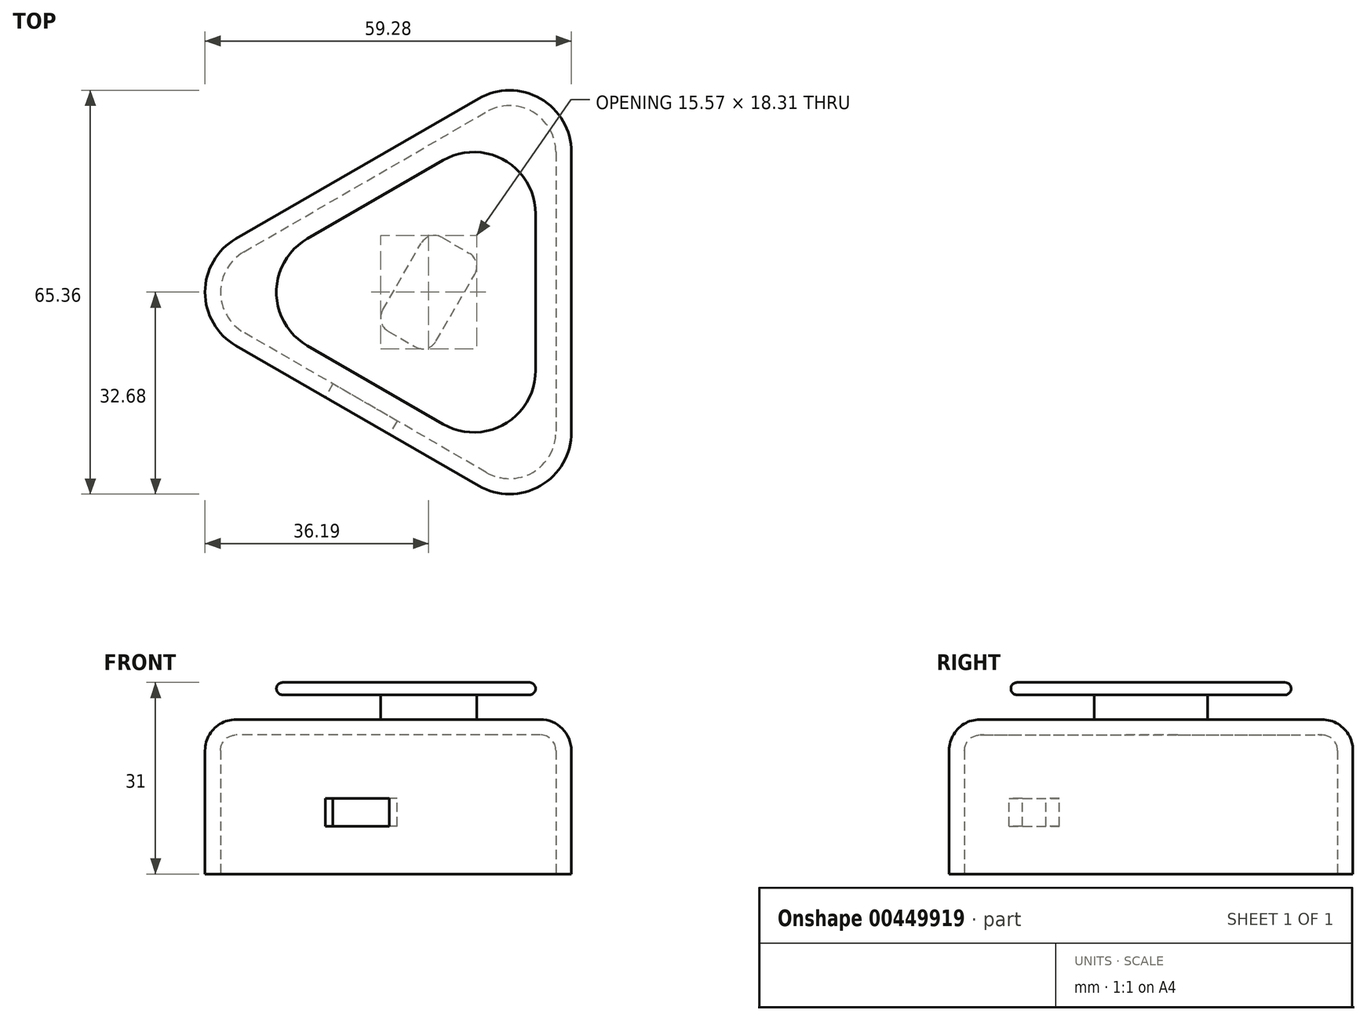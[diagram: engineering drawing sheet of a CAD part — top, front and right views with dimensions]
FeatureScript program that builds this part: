
annotation { "Feature Type Name" : "Feature", "Feature Type Description" : "" }
export const myFeature = defineFeature(function(context is Context, id is Id, definition is map)
    precondition{}
    {
        {
            var Q0;
            Q0=qCreatedBy(makeId("Top.planeOp"),FACE);
            var sketch = newSketch(context, id + "F0", { "sketchPlane" : qUnion([Q0])});
            skCircle(sketch, "E0.cCircle", {"center": v(0, 0) * mm, "radius": 23.1 * mm, "construction": true});
            skLineSegment(sketch, "E0.0", {"start": v(23.1, 40) * mm, "end": v(23.1, -40) * mm});
            skLineSegment(sketch, "E0.1", {"start": v(23.1, -40) * mm, "end": v(-46.19, 0) * mm});
            skLineSegment(sketch, "E0.2", {"start": v(-46.19, 0) * mm, "end": v(23.1, 40) * mm});
            skPoint(sketch, "E0.0.midPoint", {"position": v(23.1, 0) * mm});
            skSolve(sketch);
        }
        {
            var Q0;
            Q0=makeQuery(id+"F0.imprint","IMPRINT",FACE,{"disambiguationData":[TD([[makeQuery(id+"F0.imprint","IMPRINT",EDGE,{"derivedFrom":sQuery(id+"F0.wireOp",EDGE,"E0.0")}),-1.0]])]});
            extrude(context, id + "F1", {"entities" : qUnion([Q0]), "depth" : 25 * mm, "offsetDistance" : 25 * mm});
        }
        {
            var Q0;
            Q0=makeQuery(id+"F1.opExtrude","SWEPT_EDGE",EDGE,{"disambiguationData":[OSD([sQuery(id+"F0.wireOp",EDGE,"E0.1"),sQuery(id+"F0.wireOp",EDGE,"E0.2")])]});
            var Q1;
            Q1=makeQuery(id+"F1.opExtrude","SWEPT_EDGE",EDGE,{"disambiguationData":[OSD([sQuery(id+"F0.wireOp",EDGE,"E0.0"),sQuery(id+"F0.wireOp",EDGE,"E0.1")])]});
            var Q2;
            Q2=makeQuery(id+"F1.opExtrude","SWEPT_EDGE",EDGE,{"disambiguationData":[OSD([sQuery(id+"F0.wireOp",EDGE,"E0.0"),sQuery(id+"F0.wireOp",EDGE,"E0.2")])]});
            fillet(context, id + "F2", {"entities" : qUnion([Q0, Q1, Q2]), "radius" : 10 * mm, "tangentPropagation" : true, "allowEdgeOverflow" : false});
        }
        {
            var Q0;
            Q0=makeQuery(id+"F1.opExtrude","CAP_EDGE",EDGE,{"disambiguationData":[OSD([sQuery(id+"F0.wireOp",EDGE,"E0.1")])],"isStart":false});
            fillet(context, id + "F3", {"entities" : qUnion([Q0]), "radius" : 5 * mm, "tangentPropagation" : true, "allowEdgeOverflow" : false});
        }
        {
            var Q0;
            Q0=makeQuery(id+"F1.opExtrude","CAP_FACE",FACE,{"disambiguationData":[OSD([sQuery(id+"F0.wireOp",EDGE,"E0.0"),sQuery(id+"F0.wireOp",EDGE,"E0.1"),sQuery(id+"F0.wireOp",EDGE,"E0.2")])],"isStart":true});
            shell(context, id + "F4", {"entities" : qUnion([Q0]), "thickness" : 2.5 * mm});
        }
        {
            var Q0;
            Q0=makeQuery(id+"F1.opExtrude","CAP_FACE",FACE,{"disambiguationData":[OSD([sQuery(id+"F0.wireOp",EDGE,"E0.0"),sQuery(id+"F0.wireOp",EDGE,"E0.1"),sQuery(id+"F0.wireOp",EDGE,"E0.2")])],"isStart":false});
            var sketch = newSketch(context, id + "F5", { "sketchPlane" : qUnion([Q0])});
            skLineSegment(sketch, "E1.bottom", {"start": v(-8.7, -5.08) * mm, "end": v(0.04, 10.08) * mm});
            skLineSegment(sketch, "E1.top", {"start": v(-0.04, -10.08) * mm, "end": v(8.7, 5.08) * mm});
            skLineSegment(sketch, "E1.left", {"start": v(-8.7, -5.08) * mm, "end": v(-0.04, -10.08) * mm});
            skLineSegment(sketch, "E1.right", {"start": v(0.04, 10.08) * mm, "end": v(8.7, 5.08) * mm});
            skPoint(sketch, "E1.middle", {"position": v(0, 0) * mm});
            skSolve(sketch);
        }
        {
            var Q0;
            Q0=makeQuery(id+"F5.imprint","IMPRINT",FACE,{"disambiguationData":[TD([[makeQuery(id+"F5.imprint","IMPRINT",EDGE,{"derivedFrom":sQuery(id+"F5.wireOp",EDGE,"E1.bottom")}),-1.0]])]});
            extrude(context, id + "F6", {"entities" : qUnion([Q0]), "operationType" : NewBodyOperationType.ADD, "depth" : 4 * mm, "offsetDistance" : 25 * mm});
        }
        {
            var Q0;
            Q0=makeQuery(id+"F6.opExtrude","SWEPT_EDGE",EDGE,{"disambiguationData":[OSD([sQuery(id+"F5.wireOp",EDGE,"E1.top"),sQuery(id+"F5.wireOp",EDGE,"E1.right")])]});
            var Q1;
            Q1=makeQuery(id+"F6.opExtrude","SWEPT_EDGE",EDGE,{"disambiguationData":[OSD([sQuery(id+"F5.wireOp",EDGE,"E1.bottom"),sQuery(id+"F5.wireOp",EDGE,"E1.right")])]});
            var Q2;
            Q2=makeQuery(id+"F6.opExtrude","SWEPT_EDGE",EDGE,{"disambiguationData":[OSD([sQuery(id+"F5.wireOp",EDGE,"E1.top"),sQuery(id+"F5.wireOp",EDGE,"E1.left")])]});
            var Q3;
            Q3=makeQuery(id+"F6.opExtrude","SWEPT_EDGE",EDGE,{"disambiguationData":[OSD([sQuery(id+"F5.wireOp",EDGE,"E1.bottom"),sQuery(id+"F5.wireOp",EDGE,"E1.left")])]});
            fillet(context, id + "F7", {"entities" : qUnion([Q0, Q1, Q2, Q3]), "radius" : 2.5 * mm, "tangentPropagation" : true, "allowEdgeOverflow" : false});
        }
        {
            var Q0;
            Q0=makeQuery(id+"F6.opExtrude","CAP_FACE",FACE,{"disambiguationData":[OSD([sQuery(id+"F5.wireOp",EDGE,"E1.bottom"),sQuery(id+"F5.wireOp",EDGE,"E1.top"),sQuery(id+"F5.wireOp",EDGE,"E1.left"),sQuery(id+"F5.wireOp",EDGE,"E1.right")])],"isStart":false});
            var sketch = newSketch(context, id + "F8", { "sketchPlane" : qUnion([Q0])});
            skCircle(sketch, "E2.cCircle", {"center": v(0, 0) * mm, "radius": 17.32 * mm, "construction": true});
            skLineSegment(sketch, "E2.0", {"start": v(17.32, 30) * mm, "end": v(17.32, -30) * mm});
            skLineSegment(sketch, "E2.1", {"start": v(17.32, -30) * mm, "end": v(-34.64, 0) * mm});
            skLineSegment(sketch, "E2.2", {"start": v(-34.64, 0) * mm, "end": v(17.32, 30) * mm});
            skPoint(sketch, "E2.0.midPoint", {"position": v(17.32, 0) * mm});
            skSolve(sketch);
        }
        {
            var Q0;
            Q0=makeQuery(id+"F8.imprint","IMPRINT",FACE,{"disambiguationData":[TD([[makeQuery(id+"F8.imprint","IMPRINT",EDGE,{"derivedFrom":sQuery(id+"F8.wireOp",EDGE,"E2.0")}),-1.0]])]});
            var Q1;
            {var subQ3=sQuery(id+"F5.wireOp",EDGE,"E1.bottom");Q1=makeQuery(id+"F8.imprint","IMPRINT",FACE,{"disambiguationData":[TD([[makeQuery(id+"F8.imprint","IMPRINT",EDGE,{"derivedFrom":makeQuery(id+"F6.opExtrude","CAP_EDGE",EDGE,{"disambiguationData":[OSD([subQ3])],"isStart":false})}),-1.0]])]});}
            extrude(context, id + "F9", {"entities" : qUnion([Q0, Q1]), "operationType" : NewBodyOperationType.ADD, "depth" : 2 * mm, "offsetDistance" : 25 * mm});
        }
        {
            var Q0;
            Q0=makeQuery(id+"F9.opExtrude","SWEPT_EDGE",EDGE,{"disambiguationData":[OSD([sQuery(id+"F8.wireOp",EDGE,"E2.1"),sQuery(id+"F8.wireOp",EDGE,"E2.2")])]});
            var Q1;
            Q1=makeQuery(id+"F9.opExtrude","SWEPT_EDGE",EDGE,{"disambiguationData":[OSD([sQuery(id+"F8.wireOp",EDGE,"E2.0"),sQuery(id+"F8.wireOp",EDGE,"E2.2")])]});
            var Q2;
            Q2=makeQuery(id+"F9.opExtrude","SWEPT_EDGE",EDGE,{"disambiguationData":[OSD([sQuery(id+"F8.wireOp",EDGE,"E2.0"),sQuery(id+"F8.wireOp",EDGE,"E2.1")])]});
            fillet(context, id + "F10", {"entities" : qUnion([Q0, Q1, Q2]), "radius" : 10 * mm, "tangentPropagation" : true, "allowEdgeOverflow" : false});
        }
        {
            var Q0;
            Q0=makeQuery(id+"F9.opExtrude","CAP_EDGE",EDGE,{"disambiguationData":[OSD([sQuery(id+"F8.wireOp",EDGE,"E2.2")])],"isStart":false});
            fillet(context, id + "F11", {"entities" : qUnion([Q0]), "radius" : 1 * mm, "tangentPropagation" : true, "allowEdgeOverflow" : false});
        }
        {
            var Q0;
            Q0=makeQuery(id+"F9.opExtrude","CAP_EDGE",EDGE,{"disambiguationData":[OSD([sQuery(id+"F8.wireOp",EDGE,"E2.2")])],"isStart":true});
            fillet(context, id + "F12", {"entities" : qUnion([Q0]), "radius" : 1 * mm, "tangentPropagation" : true, "allowEdgeOverflow" : false});
        }
        {
            var Q0;
            Q0=makeQuery(id+"F1.opExtrude","SWEPT_FACE",FACE,{"disambiguationData":[OSD([sQuery(id+"F0.wireOp",EDGE,"E0.1")])]});
            var sketch = newSketch(context, id + "F13", { "sketchPlane" : qUnion([Q0])});
            skLineSegment(sketch, "E3.bottom", {"start": v(6, 7.75) * mm, "end": v(-6, 7.75) * mm});
            skLineSegment(sketch, "E3.top", {"start": v(6, 12.25) * mm, "end": v(-6, 12.25) * mm});
            skLineSegment(sketch, "E3.left", {"start": v(6, 7.75) * mm, "end": v(6, 12.25) * mm});
            skLineSegment(sketch, "E3.right", {"start": v(-6, 7.75) * mm, "end": v(-6, 12.25) * mm});
            skPoint(sketch, "E3.middle", {"position": v(0, 10) * mm});
            skSolve(sketch);
        }
        {
            var Q0;
            Q0=makeQuery(id+"F13.imprint","IMPRINT",FACE,{"disambiguationData":[TD([[makeQuery(id+"F13.imprint","IMPRINT",EDGE,{"derivedFrom":sQuery(id+"F13.wireOp",EDGE,"E3.bottom")}),-1.0]])]});
            extrude(context, id + "F14", {"entities" : qUnion([Q0]), "operationType" : NewBodyOperationType.REMOVE, "oppositeDirection" : true, "depth" : 2.5 * mm, "offsetDistance" : 25 * mm});
        }
    });
